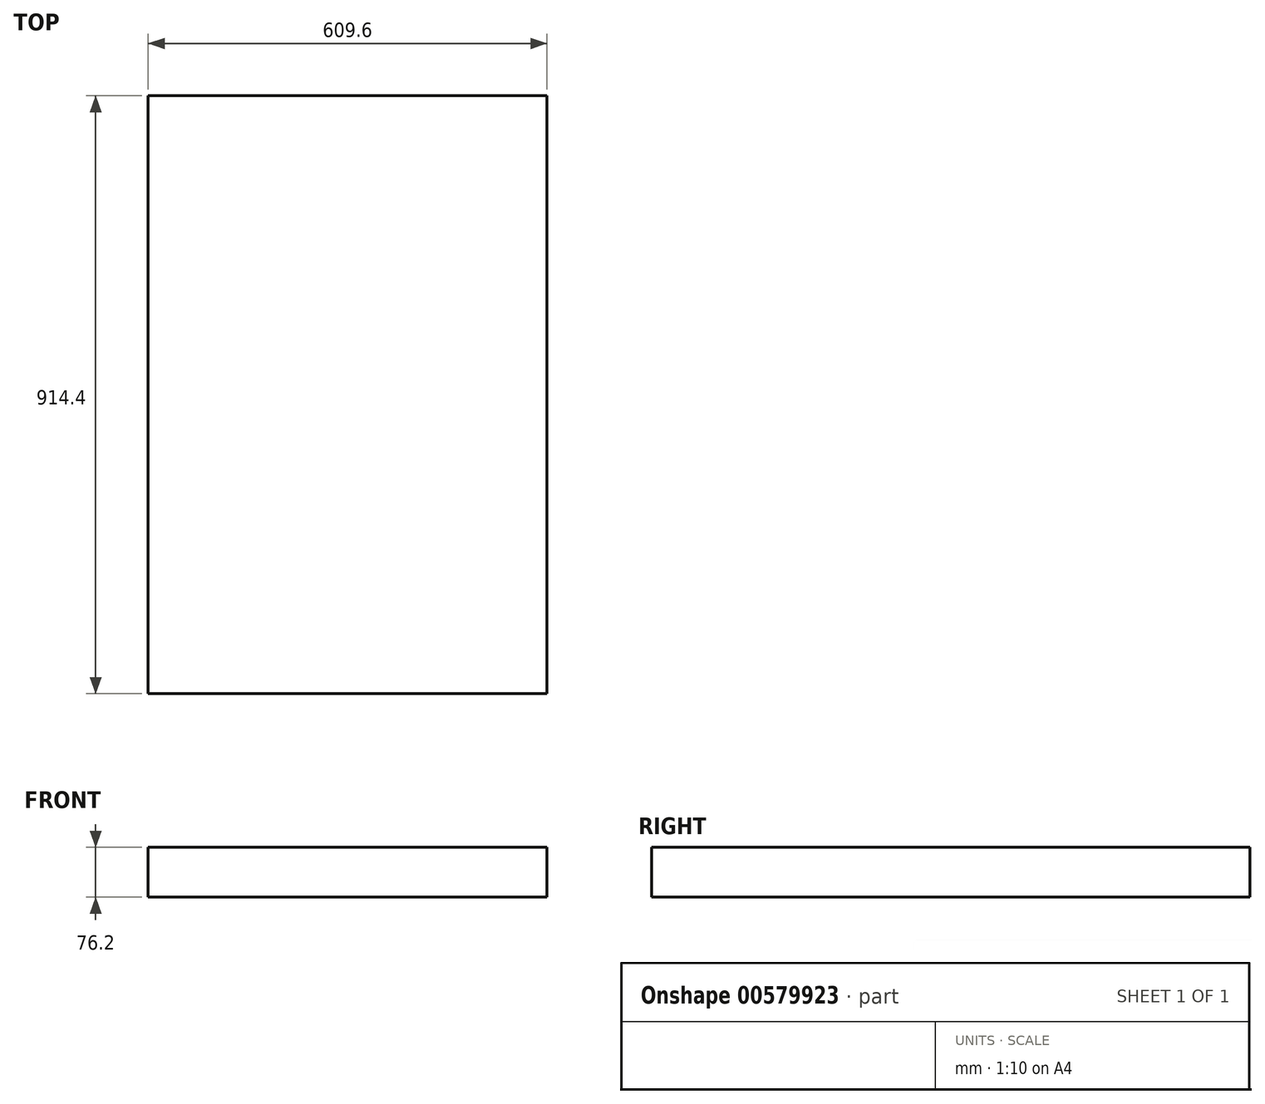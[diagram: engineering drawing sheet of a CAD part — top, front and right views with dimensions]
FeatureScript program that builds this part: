
annotation { "Feature Type Name" : "Feature", "Feature Type Description" : "" }
export const myFeature = defineFeature(function(context is Context, id is Id, definition is map)
    precondition{}
    {
        {
            var Q0;
            Q0=qCreatedBy(makeId("Top.planeOp"),FACE);
            var sketch = newSketch(context, id + "F0", { "sketchPlane" : qUnion([Q0])});
            skLineSegment(sketch, "E0.bottom", {"start": v(-355.74, 532.34) * mm, "end": v(253.86, 532.34) * mm});
            skLineSegment(sketch, "E0.top", {"start": v(-355.74, -382.06) * mm, "end": v(253.86, -382.06) * mm});
            skLineSegment(sketch, "E0.left", {"start": v(-355.74, 532.34) * mm, "end": v(-355.74, -382.06) * mm});
            skLineSegment(sketch, "E0.right", {"start": v(253.86, 532.34) * mm, "end": v(253.86, -382.06) * mm});
            skSolve(sketch);
        }
        {
            var Q0;
            Q0=makeQuery(id+"F0.imprint","IMPRINT",FACE,{"disambiguationData":[TD([[makeQuery(id+"F0.imprint","IMPRINT",EDGE,{"derivedFrom":sQuery(id+"F0.wireOp",EDGE,"E0.bottom")}),-1.0]])]});
            extrude(context, id + "F1", {"entities" : qUnion([Q0]), "depth" : 76.2 * mm, "offsetDistance" : 25.4 * mm});
        }
    });
